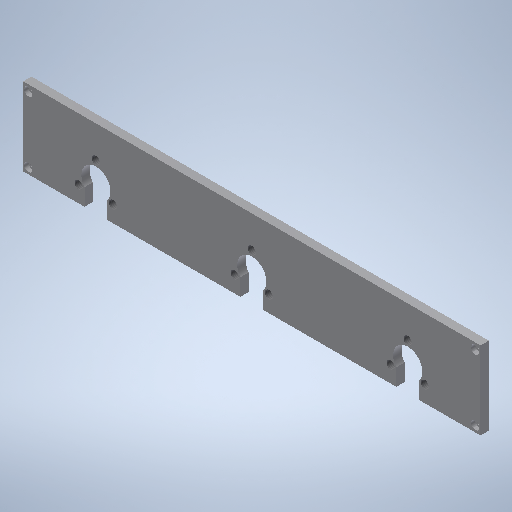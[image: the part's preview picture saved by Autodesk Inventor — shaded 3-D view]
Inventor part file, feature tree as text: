
AUTODESK INVENTOR PART (.ipt)
format: ipt  version: 2025 (Build 290162000, 162)  size: 322,560 bytes
history: native  units: in
note: dims shown in document units (in); Inventor stores cm internally (conversion verified against a paired STEP export)
features: sketch x7, extrude x2, hole x2
ambient origin geometry x8: Origin, YZ Plane, XZ Plane, XY Plane, X Axis, Y Axis, Z Axis, Center Point
bodies: Solid1 (feature_tree)
feature tree (11):
  extrude  "Extrusion1"  Depth=17.3228in
  extrude  "Extrusion4"  Depth=0.8661in
  hole  "Hole1"  [1 undecoded]
  hole  "Hole2"  [1 undecoded]
  sketch  "Sketch1"  dims[d0=2.9528in d1=17.3228in]
  sketch  "Sketch2"  dims[d5=0.4331in d7=0.9843in]
  sketch  "Sketch Rectangular Pattern1"  dims[d2=0.315in d3=0.0in d4=0.8661in]
  sketch  "Sketch3"  dims[d12=0.3937in d14=1.0in d15=1.1811in d17=5.9055in]
  sketch  "Sketch4"  dims[d35=0.307in d36=0.75in d37=0.375in d38=0.25in d39=0.5635in d40=0.2in d41=0.8108in d42=0.2362in d44=0.1969in d45=0.1969in d46=0.1772in d47=0.75in d48=0.315in d49=0.1575in d50=0.5635in d51=1.0in d52=0.8108in d58=17.3228in d59=1.4961in d60=1.1811in d62=360.0deg d64=1.1811in d66=5.9055in d67=0.3937in d69=0.3937in d71=2.7165in]
  sketch  "Sketch Circular Pattern2"  dims[d8=1.1024in d9=2.7559in]
  sketch  "Sketch Rectangular Pattern3"  dims[d21=0.25in d22=0.0in]
note: 2 required parameter values undecoded (feature->parameter linkage not recoverable at this tier; creation-order binding heuristic only, values carry confidence <= 0.55)
